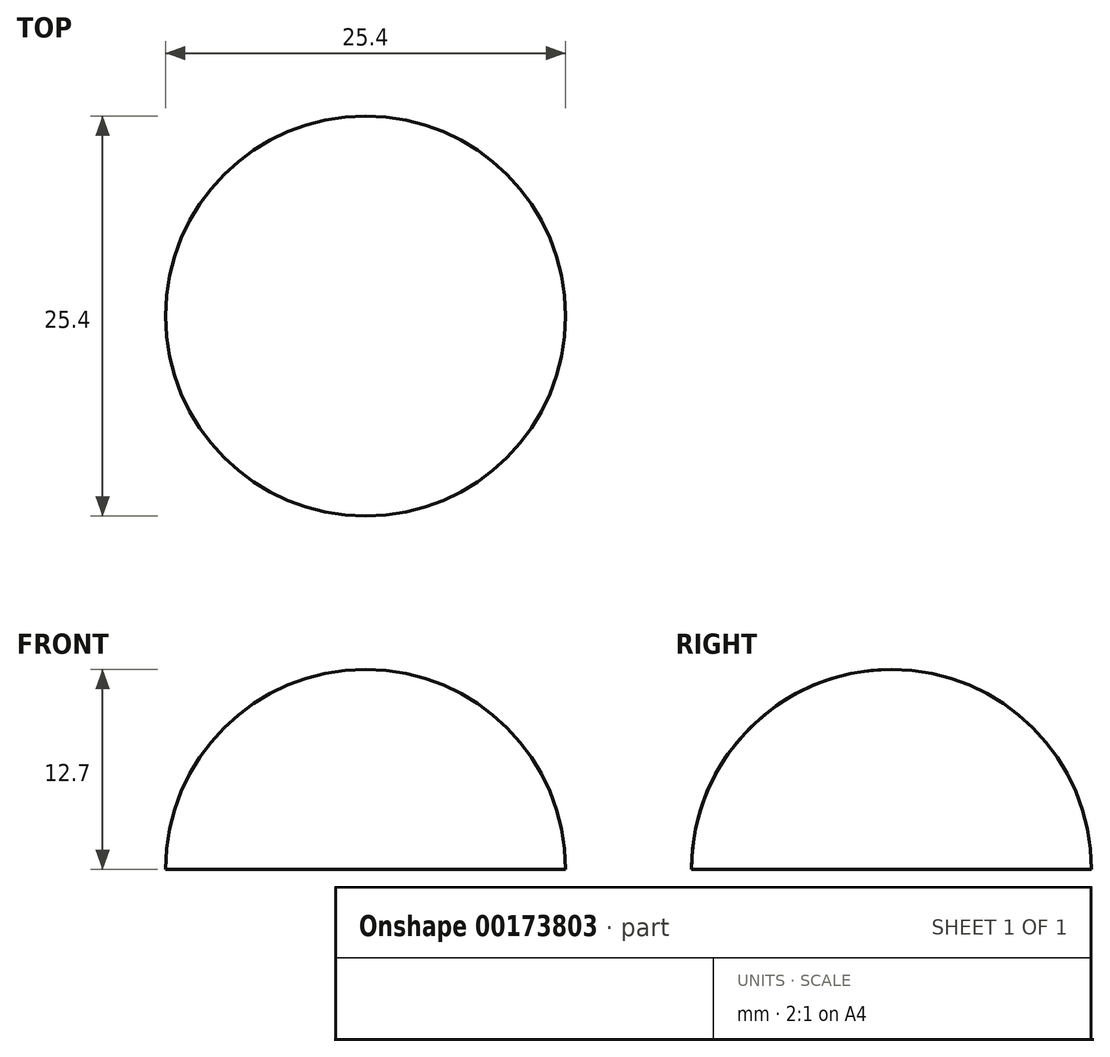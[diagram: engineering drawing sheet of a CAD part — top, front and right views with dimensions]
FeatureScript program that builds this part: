
annotation { "Feature Type Name" : "Feature", "Feature Type Description" : "" }
export const myFeature = defineFeature(function(context is Context, id is Id, definition is map)
    precondition{}
    {
        {
            var Q0;
            Q0=qCreatedBy(makeId("Right.planeOp"),FACE);
            var sketch = newSketch(context, id + "F0", { "sketchPlane" : qUnion([Q0])});
            skLineSegment(sketch, "E0", {"start": v(0, 0) * mm, "end": v(-12.7, 0) * mm});
            skArc(sketch, "E1", {"start": v(0, 12.7) * mm, "mid": v(-8.98, 8.98) * mm, "end": v(-12.7, 0) * mm});
            skLineSegment(sketch, "E2", {"start": v(0, 0) * mm, "end": v(0, 12.7) * mm});
            skSolve(sketch);
        }
        {
            var Q0;
            Q0=makeQuery(id+"F0.imprint","IMPRINT",FACE,{"disambiguationData":[TD([[makeQuery(id+"F0.imprint","IMPRINT",EDGE,{"derivedFrom":sQuery(id+"F0.wireOp",EDGE,"E0")}),-1.0]])]});
            var Q1;
            Q1=sQuery(id+"F0.wireOp",EDGE,"E2");
            revolve(context, id + "F1", {"entities" : qUnion([Q0]), "axis" : qUnion([Q1]), "revolveType" : RevolveType.FULL});
        }
    });
